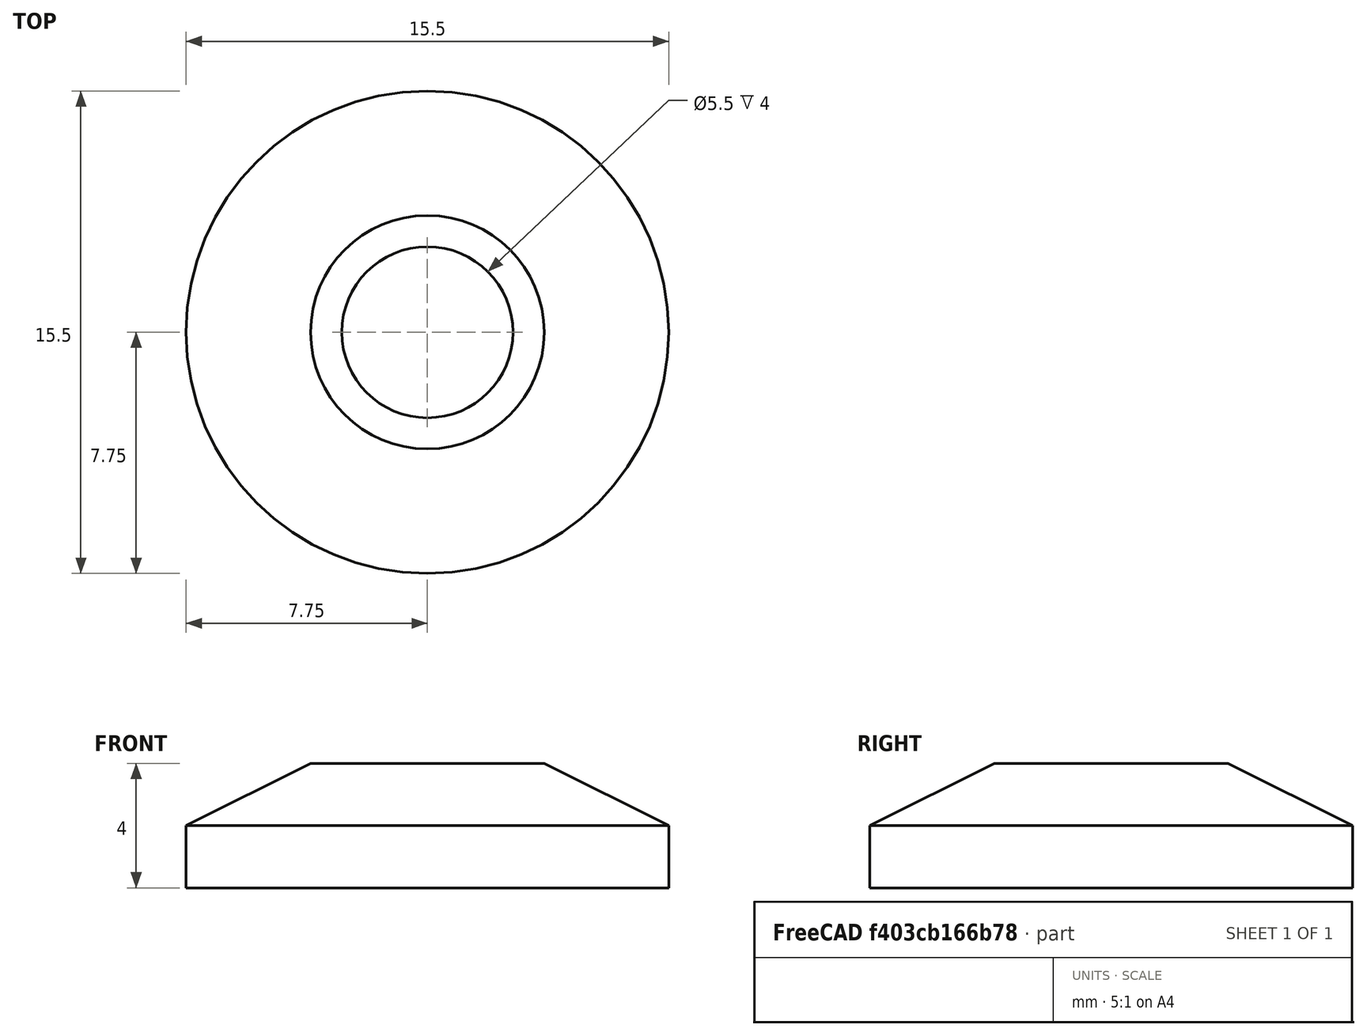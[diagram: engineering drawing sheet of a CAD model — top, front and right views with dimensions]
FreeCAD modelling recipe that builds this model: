
FCSTD DOCUMENT  (FreeCAD 0.19R)
Label: x-axis-pulley-spacer
License: All rights reserved
LicenseURL: http://en.wikipedia.org/wiki/All_rights_reserved
objects: Sketcher::SketchObject×1, PartDesign::Revolution×1, PartDesign::Body×1
note: 4 computed .brp shape members not serialized (recipe doc carries the construction recipe); baked Part::Feature solids carry a one-line shape summary decoded from their .brp

FEATURE [Sketcher::SketchObject] Sketch
  FullyConstrained = true
  MapMode = 5
  Placement = pos=(0,0,0) rot=(1,0,0;1.5708rad)
  Support = -> [XZ_Plane]
  sketch-geometry (5):
    g0: LineSegment StartX=2.75 StartY=0 StartZ=0 EndX=2.75 EndY=4 EndZ=0
    g1: LineSegment StartX=2.75 StartY=4 StartZ=0 EndX=3.75 EndY=4 EndZ=0
    g2: LineSegment StartX=3.75 StartY=4 StartZ=0 EndX=7.75 EndY=2 EndZ=0
    g3: LineSegment StartX=7.75 StartY=2 StartZ=0 EndX=7.75 EndY=0 EndZ=0
    g4: LineSegment StartX=7.75 StartY=0 StartZ=0 EndX=2.75 EndY=0 EndZ=0
  constraints (15):
    c: PointOnObject(g0,g-1)
    c: Vertical(g0)
    c: Coincident(g1,g0)
    c: Horizontal(g1)
    c: Coincident(g2,g1)
    c: Coincident(g3,g2)
    c: PointOnObject(g3,g-1)
    c: Vertical(g3)
    c: Coincident(g4,g3)
    c: Coincident(g4,g0)
    c: DistanceY(g3,g3) = 2
    c: DistanceY(g0,g0) = 4
    c: DistanceX(g-1,g0) = 2.75
    c: DistanceX(g4,g4) = 5
    c: DistanceX(g1,g1) = 1
FEATURE [PartDesign::Revolution] Revolution
  Angle = 360
  Axis = (0,-2e-16,1)
  Base = (0,0,0)
  Placement = pos=(0,0,0) rot=(1,0,0;1.5708rad)
  Profile = -> Sketch
  ReferenceAxis = -> Sketch [V_Axis]
  Reversed = true
FEATURE [PartDesign::Body] Body
  Group = -> [Sketch,Revolution]
  Origin = -> Origin
  Tip = -> Revolution
